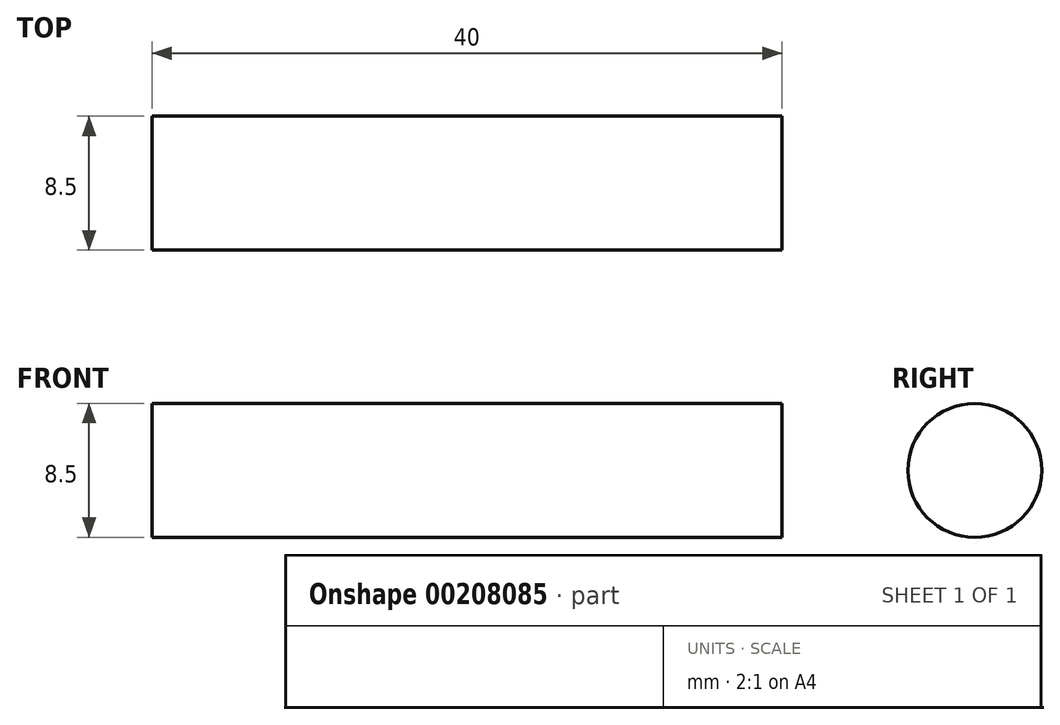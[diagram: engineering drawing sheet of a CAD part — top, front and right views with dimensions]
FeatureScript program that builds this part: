
annotation { "Feature Type Name" : "Feature", "Feature Type Description" : "" }
export const myFeature = defineFeature(function(context is Context, id is Id, definition is map)
    precondition{}
    {
        {
            var Q0;
            Q0=qCreatedBy(makeId("Top.planeOp"),FACE);
            var sketch = newSketch(context, id + "F0", { "sketchPlane" : qUnion([Q0])});
            skLineSegment(sketch, "E0.bottom", {"start": v(21, -21) * mm, "end": v(-21, -21) * mm, "construction": true});
            skLineSegment(sketch, "E0.top", {"start": v(21, 21) * mm, "end": v(-21, 21) * mm, "construction": true});
            skLineSegment(sketch, "E0.left", {"start": v(21, -21) * mm, "end": v(21, 21) * mm, "construction": true});
            skLineSegment(sketch, "E0.right", {"start": v(-21, -21) * mm, "end": v(-21, 21) * mm, "construction": true});
            skPoint(sketch, "E0.middle", {"position": v(0, 0) * mm});
            skLineSegment(sketch, "E1.bottom", {"start": v(15.5, -15.5) * mm, "end": v(-15.5, -15.5) * mm, "construction": true});
            skLineSegment(sketch, "E1.top", {"start": v(15.5, 15.5) * mm, "end": v(-15.5, 15.5) * mm, "construction": true});
            skLineSegment(sketch, "E1.left", {"start": v(15.5, -15.5) * mm, "end": v(15.5, 15.5) * mm, "construction": true});
            skLineSegment(sketch, "E1.right", {"start": v(-15.5, -15.5) * mm, "end": v(-15.5, 15.5) * mm, "construction": true});
            skCircle(sketch, "E2", {"center": v(0, 0) * mm, "radius": 13 * mm});
            skCircle(sketch, "E3", {"center": v(-15.5, -15.5) * mm, "radius": 2 * mm});
            skCircle(sketch, "E4", {"center": v(15.5, -15.5) * mm, "radius": 2 * mm});
            skCircle(sketch, "E5", {"center": v(15.5, 15.5) * mm, "radius": 2 * mm});
            skCircle(sketch, "E6", {"center": v(-15.5, 15.5) * mm, "radius": 2 * mm});
            skLineSegment(sketch, "E7.bottom", {"start": v(20, -19.5) * mm, "end": v(-20, -19.5) * mm, "construction": true});
            skLineSegment(sketch, "E7.top", {"start": v(20, 19.5) * mm, "end": v(-20, 19.5) * mm, "construction": true});
            skLineSegment(sketch, "E7.left", {"start": v(20, -19.5) * mm, "end": v(20, 19.5) * mm});
            skLineSegment(sketch, "E7.right", {"start": v(-20, -19.5) * mm, "end": v(-20, 19.5) * mm});
            skLineSegment(sketch, "E8", {"start": v(0, 0) * mm, "end": v(-28.5, 0) * mm, "construction": true});
            skLineSegment(sketch, "E9", {"start": v(0, 0) * mm, "end": v(0, 30.15) * mm, "construction": true});
            skPoint(sketch, "E9.endSnap0", {"position": v(0, 19.5) * mm});
            skLineSegment(sketch, "E10", {"start": v(-20, 19.5) * mm, "end": v(-20, 35) * mm});
            skLineSegment(sketch, "E11", {"start": v(-20, 35) * mm, "end": v(20, 35) * mm});
            skLineSegment(sketch, "E12", {"start": v(20, 35) * mm, "end": v(20, 19.5) * mm});
            skLineSegment(sketch, "E13.MirrorCS", {"start": v(-20, -35) * mm, "end": v(20, -35) * mm});
            skLineSegment(sketch, "E14.MirrorCS", {"start": v(-20, -19.5) * mm, "end": v(-20, -35) * mm});
            skLineSegment(sketch, "E15.MirrorCS", {"start": v(20, -35) * mm, "end": v(20, -19.5) * mm});
            skCircle(sketch, "E16", {"center": v(-15.5, 0) * mm, "radius": 2 * mm});
            skCircle(sketch, "E17.1.0", {"center": v(-7.75, -13.42) * mm, "radius": 2 * mm});
            skCircle(sketch, "E17.2.0", {"center": v(7.75, -13.42) * mm, "radius": 2 * mm});
            skCircle(sketch, "E17.3.0", {"center": v(15.5, 0) * mm, "radius": 2 * mm});
            skCircle(sketch, "E17.4.0", {"center": v(7.75, 13.42) * mm, "radius": 2 * mm});
            skCircle(sketch, "E17.5.0", {"center": v(-7.75, 13.42) * mm, "radius": 2 * mm});
            skSolve(sketch);
        }
        {
            var Q0;
            Q0=makeQuery(id+"F0.imprint","IMPRINT",FACE,{"disambiguationData":[TD([[makeQuery(id+"F0.imprint","IMPRINT",EDGE,{"derivedFrom":sQuery(id+"F0.wireOp",EDGE,"E2")}),-1.0]])]});
            extrude(context, id + "F1", {"entities" : qUnion([Q0]), "depth" : 15 * mm, "offsetDistance" : 25 * mm});
        }
        {
            var Q0;
            Q0=makeQuery(id+"F1.opExtrude","SWEPT_FACE",FACE,{"disambiguationData":[OSD([sQuery(id+"F0.wireOp",EDGE,"E7.left"),sQuery(id+"F0.wireOp",EDGE,"E12"),sQuery(id+"F0.wireOp",EDGE,"E15.MirrorCS")])]});
            var sketch = newSketch(context, id + "F2", { "sketchPlane" : qUnion([Q0])});
            skLineSegment(sketch, "E18", {"start": v(0, 0) * mm, "end": v(0, 15) * mm, "construction": true});
            skCircle(sketch, "E19", {"center": v(26.15, 7.5) * mm, "radius": 4.25 * mm});
            skPoint(sketch, "E19.centerSnap0", {"position": v(35, 7.5) * mm});
            skCircle(sketch, "E20.MirrorC", {"center": v(-26.15, 7.5) * mm, "radius": 4.25 * mm});
            skSolve(sketch);
        }
        {
            var Q0;
            Q0=makeQuery(id+"F2.imprint","IMPRINT",FACE,{"disambiguationData":[TD([[makeQuery(id+"F2.imprint","IMPRINT",EDGE,{"derivedFrom":sQuery(id+"F2.wireOp",EDGE,"E20.MirrorC")}),-1.0]])]});
            var Q1;
            Q1=makeQuery(id+"F2.imprint","IMPRINT",FACE,{"disambiguationData":[TD([[makeQuery(id+"F2.imprint","IMPRINT",EDGE,{"derivedFrom":sQuery(id+"F2.wireOp",EDGE,"E19")}),1.0]])]});
            extrude(context, id + "F3", {"entities" : qUnion([Q0, Q1]), "operationType" : NewBodyOperationType.REMOVE, "endBound" : BoundingType.UP_TO_NEXT, "oppositeDirection" : true, "depth" : 25 * mm, "offsetDistance" : 25 * mm});
        }
    });
